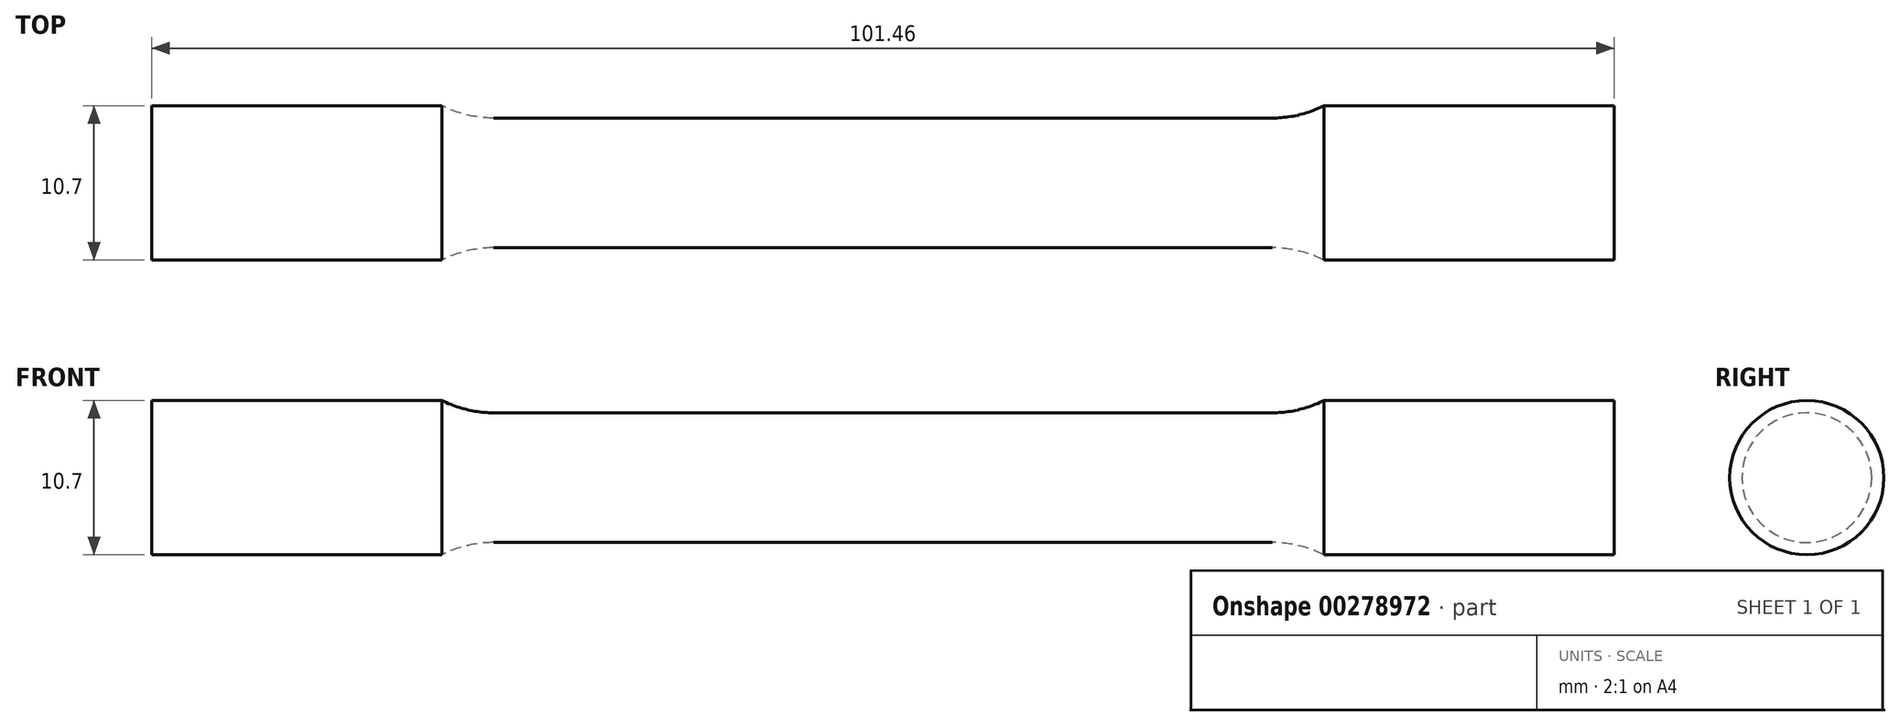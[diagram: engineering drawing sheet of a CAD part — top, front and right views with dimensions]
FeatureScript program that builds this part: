
annotation { "Feature Type Name" : "Feature", "Feature Type Description" : "" }
export const myFeature = defineFeature(function(context is Context, id is Id, definition is map)
    precondition{}
    {
        {
            var Q0;
            Q0=qCreatedBy(makeId("Front.planeOp"),FACE);
            var sketch = newSketch(context, id + "F0", { "sketchPlane" : qUnion([Q0])});
            skLineSegment(sketch, "E0", {"start": v(0, 4.5) * mm, "end": v(27, 4.5) * mm});
            skArc(sketch, "E1", {"start": v(27, 4.5) * mm, "mid": v(28.84, 4.72) * mm, "end": v(30.59, 5.35) * mm});
            skLineSegment(sketch, "E2", {"start": v(30.59, 5.35) * mm, "end": v(50.73, 5.35) * mm});
            skLineSegment(sketch, "E3", {"start": v(50.73, 5.35) * mm, "end": v(50.73, 0) * mm});
            skLineSegment(sketch, "E4.MirrorCS", {"start": v(-30.59, 5.35) * mm, "end": v(-50.73, 5.35) * mm});
            skArc(sketch, "E5.MirrorCS", {"start": v(-27, 4.5) * mm, "mid": v(-28.84, 4.72) * mm, "end": v(-30.59, 5.35) * mm});
            skLineSegment(sketch, "E6.MirrorCS", {"start": v(-50.73, 5.35) * mm, "end": v(-50.73, 0) * mm});
            skLineSegment(sketch, "E7.MirrorCS", {"start": v(0, 4.5) * mm, "end": v(-27, 4.5) * mm});
            skLineSegment(sketch, "E8", {"start": v(-50.73, 0) * mm, "end": v(50.73, 0) * mm});
            skSolve(sketch);
        }
        {
            var Q0;
            Q0=makeQuery(id+"F0.imprint","IMPRINT",FACE,{"disambiguationData":[TD([[makeQuery(id+"F0.imprint","IMPRINT",EDGE,{"derivedFrom":sQuery(id+"F0.wireOp",EDGE,"E0")}),-1.0]])]});
            var Q1;
            Q1=sQuery(id+"F0.wireOp",EDGE,"E8");
            revolve(context, id + "F1", {"entities" : qUnion([Q0]), "axis" : qUnion([Q1]), "revolveType" : RevolveType.FULL});
        }
    });
